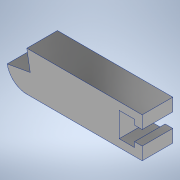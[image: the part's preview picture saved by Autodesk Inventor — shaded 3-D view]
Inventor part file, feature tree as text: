
AUTODESK INVENTOR PART (.ipt)
format: ipt  version: 2022 (Build 260153000, 153)  size: 144,384 bytes
history: native  units: mm
features: extrude x2, sketch x2
ambient origin geometry x8: Origin, YZ Plane, XZ Plane, XY Plane, X Axis, Y Axis, Z Axis, Center Point
bodies: Body1 (feature_tree)
feature tree (4):
  extrude  "Extrusion2"  Depth=6.0mm
  extrude  "Extrusion5"  Depth=12.0mm TaperAngle=0.0deg
  sketch  "Sketch5"  dims[d41=6.0mm d48=44.0mm]
  sketch  "Sketch8"  dims[d50=3.0mm d56=12.0mm d57=0.0mm d63=45.2mm d67=15.6mm d71=0.0mm d72=36.2mm d73=5.0mm d75=5.0mm d76=3.0mm d77=3.0mm d80=17.453293mm d81=1.745329mm d82=0.0mm d83=0.0mm]
